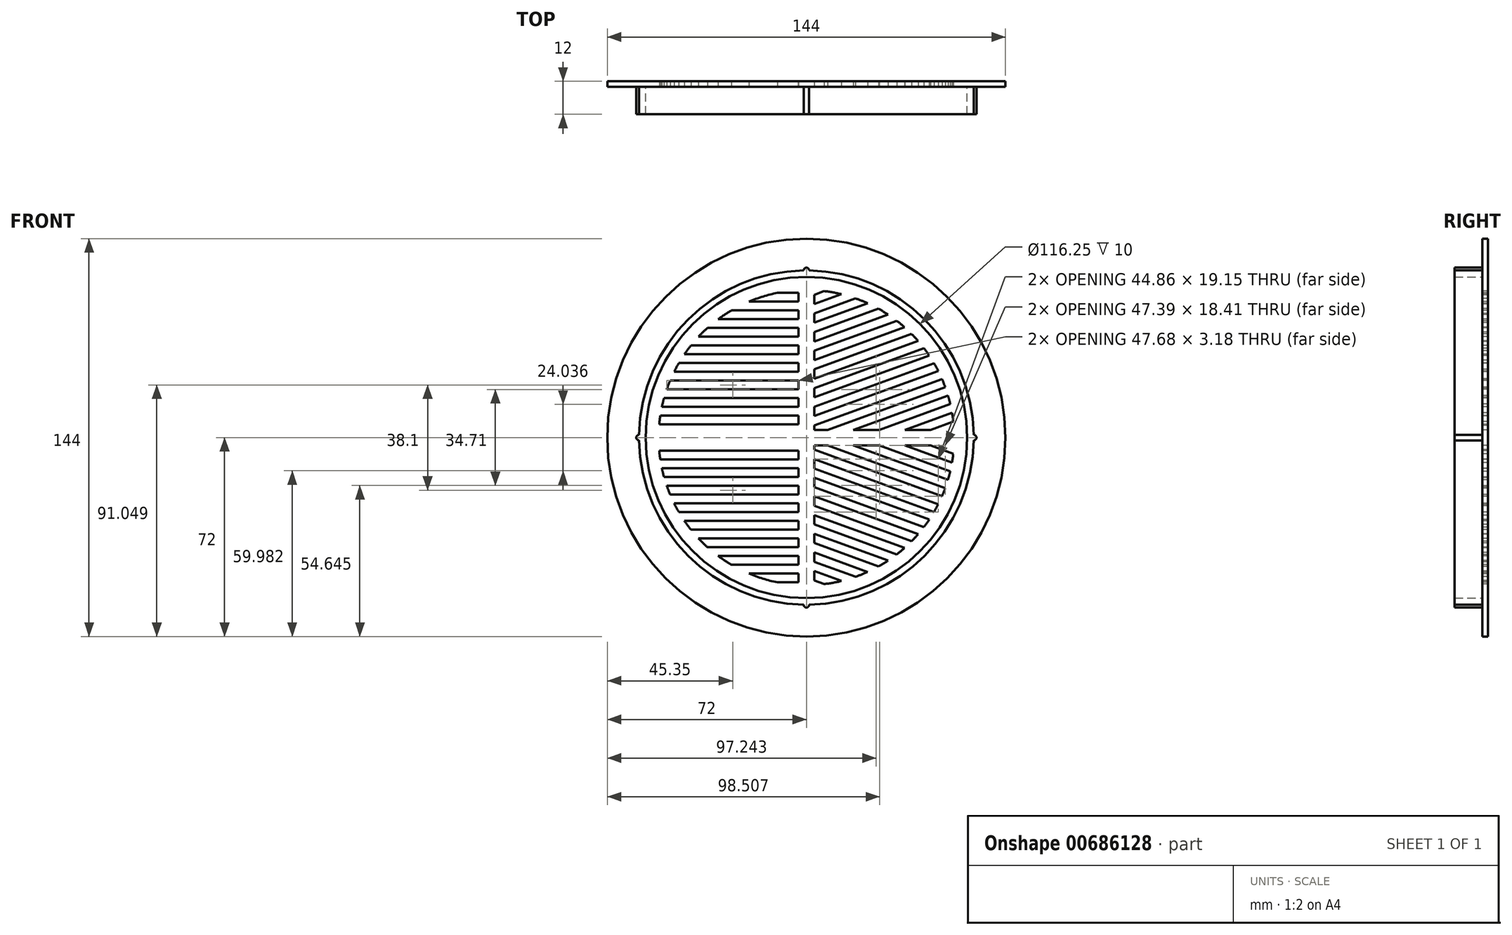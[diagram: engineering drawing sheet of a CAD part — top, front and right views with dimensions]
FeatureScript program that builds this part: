
annotation { "Feature Type Name" : "Feature", "Feature Type Description" : "" }
export const myFeature = defineFeature(function(context is Context, id is Id, definition is map)
    precondition{}
    {
        {
            var Q0;
            Q0=qCreatedBy(makeId("Front.planeOp"),FACE);
            var sketch = newSketch(context, id + "F0", { "sketchPlane" : qUnion([Q0])});
            skLineSegment(sketch, "E0", {"start": v(-20.83, -49.21) * mm, "end": v(-19.9, -49.61) * mm});
            skLineSegment(sketch, "E1", {"start": v(-19.9, -49.61) * mm, "end": v(-16.44, -50.86) * mm});
            skLineSegment(sketch, "E2", {"start": v(-16.44, -50.86) * mm, "end": v(-12.87, -51.88) * mm});
            skLineSegment(sketch, "E3", {"start": v(-12.87, -51.88) * mm, "end": v(-10.58, -52.39) * mm});
            skLineSegment(sketch, "E4", {"start": v(-10.58, -52.39) * mm, "end": v(-2.81, -52.39) * mm});
            skLineSegment(sketch, "E5", {"start": v(-2.81, -52.39) * mm, "end": v(-2.81, -49.21) * mm});
            skLineSegment(sketch, "E6", {"start": v(-2.81, -49.21) * mm, "end": v(-20.83, -49.21) * mm});
            skLineSegment(sketch, "E7", {"start": v(2.81, -48.33) * mm, "end": v(2.81, -51.7) * mm});
            skLineSegment(sketch, "E8", {"start": v(2.81, -51.7) * mm, "end": v(6.62, -53.1) * mm});
            skLineSegment(sketch, "E9", {"start": v(6.62, -53.1) * mm, "end": v(7.87, -52.94) * mm});
            skLineSegment(sketch, "E10", {"start": v(7.87, -52.94) * mm, "end": v(10.35, -52.52) * mm});
            skLineSegment(sketch, "E11", {"start": v(10.35, -52.52) * mm, "end": v(12.78, -51.98) * mm});
            skLineSegment(sketch, "E12", {"start": v(12.78, -51.98) * mm, "end": v(12.82, -51.97) * mm});
            skLineSegment(sketch, "E13", {"start": v(12.82, -51.97) * mm, "end": v(2.81, -48.33) * mm});
            skLineSegment(sketch, "E14", {"start": v(-31.9, -42.86) * mm, "end": v(-30.54, -43.86) * mm});
            skLineSegment(sketch, "E15", {"start": v(-30.54, -43.86) * mm, "end": v(-28.53, -45.2) * mm});
            skLineSegment(sketch, "E16", {"start": v(-28.53, -45.2) * mm, "end": v(-27.12, -46.04) * mm});
            skLineSegment(sketch, "E17", {"start": v(-27.12, -46.04) * mm, "end": v(-2.81, -46.04) * mm});
            skLineSegment(sketch, "E18", {"start": v(-2.81, -46.04) * mm, "end": v(-2.81, -42.86) * mm});
            skLineSegment(sketch, "E19", {"start": v(-2.81, -42.86) * mm, "end": v(-31.9, -42.86) * mm});
            skLineSegment(sketch, "E20", {"start": v(2.81, -41.57) * mm, "end": v(2.81, -44.95) * mm});
            skLineSegment(sketch, "E21", {"start": v(2.81, -44.95) * mm, "end": v(17.91, -50.44) * mm});
            skLineSegment(sketch, "E22", {"start": v(17.91, -50.44) * mm, "end": v(19.82, -49.74) * mm});
            skLineSegment(sketch, "E23", {"start": v(19.82, -49.74) * mm, "end": v(22.07, -48.78) * mm});
            skLineSegment(sketch, "E24", {"start": v(22.07, -48.78) * mm, "end": v(22.3, -48.66) * mm});
            skLineSegment(sketch, "E25", {"start": v(22.3, -48.66) * mm, "end": v(2.81, -41.57) * mm});
            skLineSegment(sketch, "E26", {"start": v(-39, -36.51) * mm, "end": v(-37.9, -37.67) * mm});
            skLineSegment(sketch, "E27", {"start": v(-37.9, -37.67) * mm, "end": v(-36.17, -39.34) * mm});
            skLineSegment(sketch, "E28", {"start": v(-36.17, -39.34) * mm, "end": v(-35.77, -39.69) * mm});
            skLineSegment(sketch, "E29", {"start": v(-35.77, -39.69) * mm, "end": v(-2.81, -39.69) * mm});
            skLineSegment(sketch, "E30", {"start": v(-2.81, -39.69) * mm, "end": v(-2.81, -36.51) * mm});
            skLineSegment(sketch, "E31", {"start": v(-2.81, -36.51) * mm, "end": v(-39, -36.51) * mm});
            skLineSegment(sketch, "E32", {"start": v(2.81, -34.81) * mm, "end": v(2.81, -38.2) * mm});
            skLineSegment(sketch, "E33", {"start": v(2.81, -38.2) * mm, "end": v(26.18, -46.7) * mm});
            skLineSegment(sketch, "E34", {"start": v(26.18, -46.7) * mm, "end": v(26.4, -46.58) * mm});
            skLineSegment(sketch, "E35", {"start": v(26.4, -46.58) * mm, "end": v(28.47, -45.34) * mm});
            skLineSegment(sketch, "E36", {"start": v(28.47, -45.34) * mm, "end": v(29.64, -44.57) * mm});
            skLineSegment(sketch, "E37", {"start": v(29.64, -44.57) * mm, "end": v(2.81, -34.81) * mm});
            skLineSegment(sketch, "E38", {"start": v(-44.11, -30.16) * mm, "end": v(-44.04, -30.28) * mm});
            skLineSegment(sketch, "E39", {"start": v(-44.04, -30.28) * mm, "end": v(-42.63, -32.23) * mm});
            skLineSegment(sketch, "E40", {"start": v(-42.63, -32.23) * mm, "end": v(-41.75, -33.34) * mm});
            skLineSegment(sketch, "E41", {"start": v(-41.75, -33.34) * mm, "end": v(-2.81, -33.34) * mm});
            skLineSegment(sketch, "E42", {"start": v(-2.81, -33.34) * mm, "end": v(-2.81, -30.16) * mm});
            skLineSegment(sketch, "E43", {"start": v(-2.81, -30.16) * mm, "end": v(-44.11, -30.16) * mm});
            skLineSegment(sketch, "E44", {"start": v(2.81, -28.05) * mm, "end": v(2.81, -31.43) * mm});
            skLineSegment(sketch, "E45", {"start": v(2.81, -31.43) * mm, "end": v(32.76, -42.33) * mm});
            skLineSegment(sketch, "E46", {"start": v(32.76, -42.33) * mm, "end": v(34.3, -41.1) * mm});
            skLineSegment(sketch, "E47", {"start": v(34.3, -41.1) * mm, "end": v(35.59, -39.98) * mm});
            skLineSegment(sketch, "E48", {"start": v(35.59, -39.98) * mm, "end": v(2.81, -28.05) * mm});
            skLineSegment(sketch, "E49", {"start": v(-47.85, -23.81) * mm, "end": v(-47.74, -24.04) * mm});
            skLineSegment(sketch, "E50", {"start": v(-47.74, -24.04) * mm, "end": v(-46.6, -26.18) * mm});
            skLineSegment(sketch, "E51", {"start": v(-46.6, -26.18) * mm, "end": v(-46.12, -26.99) * mm});
            skLineSegment(sketch, "E52", {"start": v(-46.12, -26.99) * mm, "end": v(-2.81, -26.99) * mm});
            skLineSegment(sketch, "E53", {"start": v(-2.81, -26.99) * mm, "end": v(-2.81, -23.81) * mm});
            skLineSegment(sketch, "E54", {"start": v(-2.81, -23.81) * mm, "end": v(-47.85, -23.81) * mm});
            skLineSegment(sketch, "E55", {"start": v(2.81, -21.3) * mm, "end": v(2.81, -24.67) * mm});
            skLineSegment(sketch, "E56", {"start": v(2.81, -24.67) * mm, "end": v(38.16, -37.54) * mm});
            skLineSegment(sketch, "E57", {"start": v(38.16, -37.54) * mm, "end": v(39.52, -36.12) * mm});
            skLineSegment(sketch, "E58", {"start": v(39.52, -36.12) * mm, "end": v(40.49, -35) * mm});
            skLineSegment(sketch, "E59", {"start": v(40.49, -35) * mm, "end": v(2.81, -21.3) * mm});
            skLineSegment(sketch, "E60", {"start": v(-50.52, -17.46) * mm, "end": v(-49.73, -19.6) * mm});
            skLineSegment(sketch, "E61", {"start": v(-49.73, -19.6) * mm, "end": v(-49.3, -20.64) * mm});
            skLineSegment(sketch, "E62", {"start": v(-49.3, -20.64) * mm, "end": v(-2.81, -20.64) * mm});
            skLineSegment(sketch, "E63", {"start": v(-2.81, -20.64) * mm, "end": v(-2.81, -17.46) * mm});
            skLineSegment(sketch, "E64", {"start": v(-2.81, -17.46) * mm, "end": v(-50.52, -17.46) * mm});
            skLineSegment(sketch, "E65", {"start": v(2.81, -14.54) * mm, "end": v(2.81, -17.92) * mm});
            skLineSegment(sketch, "E66", {"start": v(2.81, -17.92) * mm, "end": v(42.62, -32.4) * mm});
            skLineSegment(sketch, "E67", {"start": v(42.62, -32.4) * mm, "end": v(44.02, -30.48) * mm});
            skLineSegment(sketch, "E68", {"start": v(44.02, -30.48) * mm, "end": v(44.52, -29.72) * mm});
            skLineSegment(sketch, "E69", {"start": v(44.52, -29.72) * mm, "end": v(2.81, -14.54) * mm});
            skLineSegment(sketch, "E70", {"start": v(-52.27, -11.11) * mm, "end": v(-51.96, -12.55) * mm});
            skLineSegment(sketch, "E71", {"start": v(-51.96, -12.55) * mm, "end": v(-51.5, -14.29) * mm});
            skLineSegment(sketch, "E72", {"start": v(-51.5, -14.29) * mm, "end": v(-2.81, -14.29) * mm});
            skLineSegment(sketch, "E73", {"start": v(-2.81, -14.29) * mm, "end": v(-2.81, -11.11) * mm});
            skLineSegment(sketch, "E74", {"start": v(-2.81, -11.11) * mm, "end": v(-52.27, -11.11) * mm});
            skLineSegment(sketch, "E75", {"start": v(2.81, -7.78) * mm, "end": v(2.81, -11.16) * mm});
            skLineSegment(sketch, "E76", {"start": v(2.81, -11.16) * mm, "end": v(46.24, -26.97) * mm});
            skLineSegment(sketch, "E77", {"start": v(46.24, -26.97) * mm, "end": v(46.58, -26.4) * mm});
            skLineSegment(sketch, "E78", {"start": v(46.58, -26.4) * mm, "end": v(47.73, -24.26) * mm});
            skLineSegment(sketch, "E79", {"start": v(47.73, -24.26) * mm, "end": v(47.78, -24.15) * mm});
            skLineSegment(sketch, "E80", {"start": v(47.78, -24.15) * mm, "end": v(2.81, -7.78) * mm});
            skLineSegment(sketch, "E81", {"start": v(-53.22, -4.76) * mm, "end": v(-53.2, -5.13) * mm});
            skLineSegment(sketch, "E82", {"start": v(-53.2, -5.13) * mm, "end": v(-52.9, -7.64) * mm});
            skLineSegment(sketch, "E83", {"start": v(-52.9, -7.64) * mm, "end": v(-52.85, -7.94) * mm});
            skLineSegment(sketch, "E84", {"start": v(-52.85, -7.94) * mm, "end": v(-2.81, -7.94) * mm});
            skLineSegment(sketch, "E85", {"start": v(-2.81, -7.94) * mm, "end": v(-2.81, -4.76) * mm});
            skLineSegment(sketch, "E86", {"start": v(-2.81, -4.76) * mm, "end": v(-53.22, -4.76) * mm});
            skLineSegment(sketch, "E87", {"start": v(35.58, -2.81) * mm, "end": v(52.74, -9.06) * mm});
            skLineSegment(sketch, "E88", {"start": v(52.74, -9.06) * mm, "end": v(52.94, -7.87) * mm});
            skLineSegment(sketch, "E89", {"start": v(52.94, -7.87) * mm, "end": v(53.19, -5.84) * mm});
            skLineSegment(sketch, "E90", {"start": v(53.19, -5.84) * mm, "end": v(44.86, -2.81) * mm});
            skLineSegment(sketch, "E91", {"start": v(44.86, -2.81) * mm, "end": v(35.58, -2.81) * mm});
            skLineSegment(sketch, "E92", {"start": v(17, -2.81) * mm, "end": v(51.3, -15.3) * mm});
            skLineSegment(sketch, "E93", {"start": v(51.3, -15.3) * mm, "end": v(51.34, -15.18) * mm});
            skLineSegment(sketch, "E94", {"start": v(51.34, -15.18) * mm, "end": v(51.98, -12.78) * mm});
            skLineSegment(sketch, "E95", {"start": v(51.98, -12.78) * mm, "end": v(52.1, -12.2) * mm});
            skLineSegment(sketch, "E96", {"start": v(52.1, -12.2) * mm, "end": v(26.3, -2.81) * mm});
            skLineSegment(sketch, "E97", {"start": v(26.3, -2.81) * mm, "end": v(17, -2.81) * mm});
            skLineSegment(sketch, "E98", {"start": v(2.81, -2.81) * mm, "end": v(2.81, -4.4) * mm});
            skLineSegment(sketch, "E99", {"start": v(2.81, -4.4) * mm, "end": v(49.12, -21.26) * mm});
            skLineSegment(sketch, "E100", {"start": v(49.12, -21.26) * mm, "end": v(49.74, -19.82) * mm});
            skLineSegment(sketch, "E101", {"start": v(49.74, -19.82) * mm, "end": v(50.3, -18.3) * mm});
            skLineSegment(sketch, "E102", {"start": v(50.3, -18.3) * mm, "end": v(7.73, -2.81) * mm});
            skLineSegment(sketch, "E103", {"start": v(7.73, -2.81) * mm, "end": v(2.81, -2.81) * mm});
            skLineSegment(sketch, "E104", {"start": v(-53.4, 1.59) * mm, "end": v(-53.44, 0) * mm});
            skLineSegment(sketch, "E105", {"start": v(-53.44, 0) * mm, "end": v(-53.4, -1.59) * mm});
            skLineSegment(sketch, "E106", {"start": v(-53.4, -1.59) * mm, "end": v(-2.81, -1.59) * mm});
            skLineSegment(sketch, "E107", {"start": v(-2.81, -1.59) * mm, "end": v(-2.81, 1.59) * mm});
            skLineSegment(sketch, "E108", {"start": v(-2.81, 1.59) * mm, "end": v(-53.4, 1.59) * mm});
            skLineSegment(sketch, "E109", {"start": v(-52.85, 7.94) * mm, "end": v(-52.9, 7.64) * mm});
            skLineSegment(sketch, "E110", {"start": v(-52.9, 7.64) * mm, "end": v(-53.2, 5.13) * mm});
            skLineSegment(sketch, "E111", {"start": v(-53.2, 5.13) * mm, "end": v(-53.22, 4.76) * mm});
            skLineSegment(sketch, "E112", {"start": v(-53.22, 4.76) * mm, "end": v(-2.81, 4.76) * mm});
            skLineSegment(sketch, "E113", {"start": v(-2.81, 4.76) * mm, "end": v(-2.81, 7.94) * mm});
            skLineSegment(sketch, "E114", {"start": v(-2.81, 7.94) * mm, "end": v(-52.85, 7.94) * mm});
            skLineSegment(sketch, "E115", {"start": v(52.74, 9.06) * mm, "end": v(35.58, 2.81) * mm});
            skLineSegment(sketch, "E116", {"start": v(35.58, 2.81) * mm, "end": v(44.86, 2.81) * mm});
            skLineSegment(sketch, "E117", {"start": v(44.86, 2.81) * mm, "end": v(53.19, 5.84) * mm});
            skLineSegment(sketch, "E118", {"start": v(53.19, 5.84) * mm, "end": v(52.94, 7.87) * mm});
            skLineSegment(sketch, "E119", {"start": v(52.94, 7.87) * mm, "end": v(52.74, 9.06) * mm});
            skLineSegment(sketch, "E120", {"start": v(-51.5, 14.29) * mm, "end": v(-51.96, 12.55) * mm});
            skLineSegment(sketch, "E121", {"start": v(-51.96, 12.55) * mm, "end": v(-52.27, 11.11) * mm});
            skLineSegment(sketch, "E122", {"start": v(-52.27, 11.11) * mm, "end": v(-2.81, 11.11) * mm});
            skLineSegment(sketch, "E123", {"start": v(-2.81, 11.11) * mm, "end": v(-2.81, 14.29) * mm});
            skLineSegment(sketch, "E124", {"start": v(-2.81, 14.29) * mm, "end": v(-51.5, 14.29) * mm});
            skLineSegment(sketch, "E125", {"start": v(51.3, 15.3) * mm, "end": v(17, 2.81) * mm});
            skLineSegment(sketch, "E126", {"start": v(17, 2.81) * mm, "end": v(26.3, 2.81) * mm});
            skLineSegment(sketch, "E127", {"start": v(26.3, 2.81) * mm, "end": v(52.1, 12.2) * mm});
            skLineSegment(sketch, "E128", {"start": v(52.1, 12.2) * mm, "end": v(51.98, 12.78) * mm});
            skLineSegment(sketch, "E129", {"start": v(51.98, 12.78) * mm, "end": v(51.34, 15.18) * mm});
            skLineSegment(sketch, "E130", {"start": v(51.34, 15.18) * mm, "end": v(51.3, 15.3) * mm});
            skLineSegment(sketch, "E131", {"start": v(-49.3, 20.64) * mm, "end": v(-49.73, 19.6) * mm});
            skLineSegment(sketch, "E132", {"start": v(-49.73, 19.6) * mm, "end": v(-50.52, 17.46) * mm});
            skLineSegment(sketch, "E133", {"start": v(-50.52, 17.46) * mm, "end": v(-2.81, 17.46) * mm});
            skLineSegment(sketch, "E134", {"start": v(-2.81, 17.46) * mm, "end": v(-2.81, 20.64) * mm});
            skLineSegment(sketch, "E135", {"start": v(-2.81, 20.64) * mm, "end": v(-49.3, 20.64) * mm});
            skLineSegment(sketch, "E136", {"start": v(49.12, 21.26) * mm, "end": v(2.81, 4.4) * mm});
            skLineSegment(sketch, "E137", {"start": v(2.81, 4.4) * mm, "end": v(2.81, 2.81) * mm});
            skLineSegment(sketch, "E138", {"start": v(2.81, 2.81) * mm, "end": v(7.73, 2.81) * mm});
            skLineSegment(sketch, "E139", {"start": v(7.73, 2.81) * mm, "end": v(50.3, 18.3) * mm});
            skLineSegment(sketch, "E140", {"start": v(50.3, 18.3) * mm, "end": v(49.74, 19.82) * mm});
            skLineSegment(sketch, "E141", {"start": v(49.74, 19.82) * mm, "end": v(49.12, 21.26) * mm});
            skLineSegment(sketch, "E142", {"start": v(46.24, 26.97) * mm, "end": v(2.81, 11.16) * mm});
            skLineSegment(sketch, "E143", {"start": v(2.81, 11.16) * mm, "end": v(2.81, 7.78) * mm});
            skLineSegment(sketch, "E144", {"start": v(2.81, 7.78) * mm, "end": v(47.78, 24.15) * mm});
            skLineSegment(sketch, "E145", {"start": v(47.78, 24.15) * mm, "end": v(47.73, 24.26) * mm});
            skLineSegment(sketch, "E146", {"start": v(47.73, 24.26) * mm, "end": v(46.58, 26.4) * mm});
            skLineSegment(sketch, "E147", {"start": v(46.58, 26.4) * mm, "end": v(46.24, 26.97) * mm});
            skLineSegment(sketch, "E148", {"start": v(-46.12, 26.99) * mm, "end": v(-46.6, 26.18) * mm});
            skLineSegment(sketch, "E149", {"start": v(-46.6, 26.18) * mm, "end": v(-47.74, 24.04) * mm});
            skLineSegment(sketch, "E150", {"start": v(-47.74, 24.04) * mm, "end": v(-47.85, 23.81) * mm});
            skLineSegment(sketch, "E151", {"start": v(-47.85, 23.81) * mm, "end": v(-2.81, 23.81) * mm});
            skLineSegment(sketch, "E152", {"start": v(-2.81, 23.81) * mm, "end": v(-2.81, 26.99) * mm});
            skLineSegment(sketch, "E153", {"start": v(-2.81, 26.99) * mm, "end": v(-46.12, 26.99) * mm});
            skLineSegment(sketch, "E154", {"start": v(42.62, 32.4) * mm, "end": v(2.81, 17.92) * mm});
            skLineSegment(sketch, "E155", {"start": v(2.81, 17.92) * mm, "end": v(2.81, 14.54) * mm});
            skLineSegment(sketch, "E156", {"start": v(2.81, 14.54) * mm, "end": v(44.52, 29.72) * mm});
            skLineSegment(sketch, "E157", {"start": v(44.52, 29.72) * mm, "end": v(44.02, 30.48) * mm});
            skLineSegment(sketch, "E158", {"start": v(44.02, 30.48) * mm, "end": v(42.62, 32.4) * mm});
            skLineSegment(sketch, "E159", {"start": v(-41.75, 33.34) * mm, "end": v(-42.63, 32.23) * mm});
            skLineSegment(sketch, "E160", {"start": v(-42.63, 32.23) * mm, "end": v(-44.04, 30.28) * mm});
            skLineSegment(sketch, "E161", {"start": v(-44.04, 30.28) * mm, "end": v(-44.11, 30.16) * mm});
            skLineSegment(sketch, "E162", {"start": v(-44.11, 30.16) * mm, "end": v(-2.81, 30.16) * mm});
            skLineSegment(sketch, "E163", {"start": v(-2.81, 30.16) * mm, "end": v(-2.81, 33.34) * mm});
            skLineSegment(sketch, "E164", {"start": v(-2.81, 33.34) * mm, "end": v(-41.75, 33.34) * mm});
            skLineSegment(sketch, "E165", {"start": v(38.16, 37.54) * mm, "end": v(2.81, 24.67) * mm});
            skLineSegment(sketch, "E166", {"start": v(2.81, 24.67) * mm, "end": v(2.81, 21.3) * mm});
            skLineSegment(sketch, "E167", {"start": v(2.81, 21.3) * mm, "end": v(40.49, 35) * mm});
            skLineSegment(sketch, "E168", {"start": v(40.49, 35) * mm, "end": v(39.52, 36.12) * mm});
            skLineSegment(sketch, "E169", {"start": v(39.52, 36.12) * mm, "end": v(38.16, 37.54) * mm});
            skLineSegment(sketch, "E170", {"start": v(-35.77, 39.69) * mm, "end": v(-36.17, 39.34) * mm});
            skLineSegment(sketch, "E171", {"start": v(-36.17, 39.34) * mm, "end": v(-37.9, 37.67) * mm});
            skLineSegment(sketch, "E172", {"start": v(-37.9, 37.67) * mm, "end": v(-39, 36.51) * mm});
            skLineSegment(sketch, "E173", {"start": v(-39, 36.51) * mm, "end": v(-2.81, 36.51) * mm});
            skLineSegment(sketch, "E174", {"start": v(-2.81, 36.51) * mm, "end": v(-2.81, 39.69) * mm});
            skLineSegment(sketch, "E175", {"start": v(-2.81, 39.69) * mm, "end": v(-35.77, 39.69) * mm});
            skLineSegment(sketch, "E176", {"start": v(32.76, 42.33) * mm, "end": v(2.81, 31.43) * mm});
            skLineSegment(sketch, "E177", {"start": v(2.81, 31.43) * mm, "end": v(2.81, 28.05) * mm});
            skLineSegment(sketch, "E178", {"start": v(2.81, 28.05) * mm, "end": v(35.59, 39.98) * mm});
            skLineSegment(sketch, "E179", {"start": v(35.59, 39.98) * mm, "end": v(34.3, 41.1) * mm});
            skLineSegment(sketch, "E180", {"start": v(34.3, 41.1) * mm, "end": v(32.76, 42.33) * mm});
            skLineSegment(sketch, "E181", {"start": v(-27.12, 46.04) * mm, "end": v(-28.53, 45.2) * mm});
            skLineSegment(sketch, "E182", {"start": v(-28.53, 45.2) * mm, "end": v(-30.54, 43.86) * mm});
            skLineSegment(sketch, "E183", {"start": v(-30.54, 43.86) * mm, "end": v(-31.9, 42.86) * mm});
            skLineSegment(sketch, "E184", {"start": v(-31.9, 42.86) * mm, "end": v(-2.81, 42.86) * mm});
            skLineSegment(sketch, "E185", {"start": v(-2.81, 42.86) * mm, "end": v(-2.81, 46.04) * mm});
            skLineSegment(sketch, "E186", {"start": v(-2.81, 46.04) * mm, "end": v(-27.12, 46.04) * mm});
            skLineSegment(sketch, "E187", {"start": v(26.18, 46.7) * mm, "end": v(2.81, 38.2) * mm});
            skLineSegment(sketch, "E188", {"start": v(2.81, 38.2) * mm, "end": v(2.81, 34.81) * mm});
            skLineSegment(sketch, "E189", {"start": v(2.81, 34.81) * mm, "end": v(29.64, 44.57) * mm});
            skLineSegment(sketch, "E190", {"start": v(29.71, 44.6) * mm, "end": v(26.4, 46.58) * mm});
            skLineSegment(sketch, "E191", {"start": v(17.91, 50.44) * mm, "end": v(2.81, 44.95) * mm});
            skLineSegment(sketch, "E192", {"start": v(2.81, 44.95) * mm, "end": v(2.81, 41.57) * mm});
            skLineSegment(sketch, "E193", {"start": v(2.81, 41.57) * mm, "end": v(22.3, 48.66) * mm});
            skLineSegment(sketch, "E194", {"start": v(22.3, 48.66) * mm, "end": v(22.07, 48.78) * mm});
            skLineSegment(sketch, "E195", {"start": v(22.07, 48.78) * mm, "end": v(19.82, 49.74) * mm});
            skLineSegment(sketch, "E196", {"start": v(19.82, 49.74) * mm, "end": v(17.91, 50.44) * mm});
            skLineSegment(sketch, "E197", {"start": v(-10.58, 52.39) * mm, "end": v(-12.87, 51.88) * mm});
            skLineSegment(sketch, "E198", {"start": v(-12.87, 51.88) * mm, "end": v(-16.44, 50.86) * mm});
            skLineSegment(sketch, "E199", {"start": v(-16.44, 50.86) * mm, "end": v(-19.9, 49.6) * mm});
            skLineSegment(sketch, "E200", {"start": v(-19.9, 49.6) * mm, "end": v(-20.83, 49.21) * mm});
            skLineSegment(sketch, "E201", {"start": v(-20.83, 49.21) * mm, "end": v(-2.81, 49.21) * mm});
            skLineSegment(sketch, "E202", {"start": v(-2.81, 49.21) * mm, "end": v(-2.81, 52.39) * mm});
            skLineSegment(sketch, "E203", {"start": v(-2.81, 52.39) * mm, "end": v(-10.58, 52.39) * mm});
            skLineSegment(sketch, "E204", {"start": v(6.62, 53.1) * mm, "end": v(2.81, 51.7) * mm});
            skLineSegment(sketch, "E205", {"start": v(2.81, 51.7) * mm, "end": v(2.81, 48.33) * mm});
            skLineSegment(sketch, "E206", {"start": v(2.81, 48.33) * mm, "end": v(12.82, 51.97) * mm});
            skLineSegment(sketch, "E207", {"start": v(12.82, 51.97) * mm, "end": v(12.78, 51.98) * mm});
            skLineSegment(sketch, "E208", {"start": v(12.78, 51.98) * mm, "end": v(10.35, 52.52) * mm});
            skLineSegment(sketch, "E209", {"start": v(10.35, 52.52) * mm, "end": v(7.87, 52.94) * mm});
            skLineSegment(sketch, "E210", {"start": v(7.87, 52.94) * mm, "end": v(6.62, 53.1) * mm});
            skLineSegment(sketch, "E211", {"start": v(0, 58.13) * mm, "end": v(3, 58.05) * mm});
            skLineSegment(sketch, "E212", {"start": v(3, 58.05) * mm, "end": v(5.94, 57.82) * mm});
            skLineSegment(sketch, "E213", {"start": v(5.94, 57.82) * mm, "end": v(8.85, 57.45) * mm});
            skLineSegment(sketch, "E214", {"start": v(8.85, 57.45) * mm, "end": v(11.71, 56.94) * mm});
            skLineSegment(sketch, "E215", {"start": v(11.71, 56.94) * mm, "end": v(14.53, 56.3) * mm});
            skLineSegment(sketch, "E216", {"start": v(14.53, 56.3) * mm, "end": v(17.28, 55.51) * mm});
            skLineSegment(sketch, "E217", {"start": v(17.28, 55.51) * mm, "end": v(19.98, 54.6) * mm});
            skLineSegment(sketch, "E218", {"start": v(19.98, 54.6) * mm, "end": v(22.63, 53.56) * mm});
            skLineSegment(sketch, "E219", {"start": v(22.63, 53.56) * mm, "end": v(25.2, 52.4) * mm});
            skLineSegment(sketch, "E220", {"start": v(25.2, 52.4) * mm, "end": v(27.7, 51.1) * mm});
            skLineSegment(sketch, "E221", {"start": v(27.7, 51.1) * mm, "end": v(30.14, 49.71) * mm});
            skLineSegment(sketch, "E222", {"start": v(30.14, 49.71) * mm, "end": v(32.5, 48.2) * mm});
            skLineSegment(sketch, "E223", {"start": v(32.5, 48.2) * mm, "end": v(34.78, 46.58) * mm});
            skLineSegment(sketch, "E224", {"start": v(34.78, 46.58) * mm, "end": v(36.97, 44.85) * mm});
            skLineSegment(sketch, "E225", {"start": v(36.97, 44.85) * mm, "end": v(39.08, 43.03) * mm});
            skLineSegment(sketch, "E226", {"start": v(39.08, 43.03) * mm, "end": v(41.1, 41.1) * mm});
            skLineSegment(sketch, "E227", {"start": v(41.1, 41.1) * mm, "end": v(43.03, 39.08) * mm});
            skLineSegment(sketch, "E228", {"start": v(43.03, 39.08) * mm, "end": v(44.85, 36.97) * mm});
            skLineSegment(sketch, "E229", {"start": v(44.85, 36.97) * mm, "end": v(46.58, 34.78) * mm});
            skLineSegment(sketch, "E230", {"start": v(46.58, 34.78) * mm, "end": v(48.2, 32.5) * mm});
            skLineSegment(sketch, "E231", {"start": v(48.2, 32.5) * mm, "end": v(49.71, 30.14) * mm});
            skLineSegment(sketch, "E232", {"start": v(49.71, 30.14) * mm, "end": v(51.1, 27.7) * mm});
            skLineSegment(sketch, "E233", {"start": v(51.1, 27.7) * mm, "end": v(52.4, 25.2) * mm});
            skLineSegment(sketch, "E234", {"start": v(52.4, 25.2) * mm, "end": v(53.56, 22.63) * mm});
            skLineSegment(sketch, "E235", {"start": v(53.56, 22.63) * mm, "end": v(54.6, 19.99) * mm});
            skLineSegment(sketch, "E236", {"start": v(54.6, 19.99) * mm, "end": v(55.51, 17.28) * mm});
            skLineSegment(sketch, "E237", {"start": v(55.51, 17.28) * mm, "end": v(56.3, 14.53) * mm});
            skLineSegment(sketch, "E238", {"start": v(56.3, 14.53) * mm, "end": v(56.94, 11.71) * mm});
            skLineSegment(sketch, "E239", {"start": v(56.94, 11.71) * mm, "end": v(57.46, 8.85) * mm});
            skLineSegment(sketch, "E240", {"start": v(57.46, 8.85) * mm, "end": v(57.82, 5.94) * mm});
            skLineSegment(sketch, "E241", {"start": v(57.82, 5.94) * mm, "end": v(58.05, 3) * mm});
            skLineSegment(sketch, "E242", {"start": v(58.05, 3) * mm, "end": v(58.12, 0) * mm});
            skLineSegment(sketch, "E243", {"start": v(58.12, 0) * mm, "end": v(58.05, -3) * mm});
            skLineSegment(sketch, "E244", {"start": v(58.05, -3) * mm, "end": v(57.82, -5.94) * mm});
            skLineSegment(sketch, "E245", {"start": v(57.82, -5.94) * mm, "end": v(57.46, -8.85) * mm});
            skLineSegment(sketch, "E246", {"start": v(57.46, -8.85) * mm, "end": v(56.94, -11.71) * mm});
            skLineSegment(sketch, "E247", {"start": v(56.94, -11.71) * mm, "end": v(56.3, -14.53) * mm});
            skLineSegment(sketch, "E248", {"start": v(56.3, -14.53) * mm, "end": v(55.51, -17.28) * mm});
            skLineSegment(sketch, "E249", {"start": v(55.51, -17.28) * mm, "end": v(54.6, -19.99) * mm});
            skLineSegment(sketch, "E250", {"start": v(54.6, -19.99) * mm, "end": v(53.56, -22.63) * mm});
            skLineSegment(sketch, "E251", {"start": v(53.56, -22.63) * mm, "end": v(52.4, -25.2) * mm});
            skLineSegment(sketch, "E252", {"start": v(52.4, -25.2) * mm, "end": v(51.1, -27.7) * mm});
            skLineSegment(sketch, "E253", {"start": v(51.1, -27.7) * mm, "end": v(49.71, -30.14) * mm});
            skLineSegment(sketch, "E254", {"start": v(49.71, -30.14) * mm, "end": v(48.2, -32.5) * mm});
            skLineSegment(sketch, "E255", {"start": v(48.2, -32.5) * mm, "end": v(46.58, -34.78) * mm});
            skLineSegment(sketch, "E256", {"start": v(46.58, -34.78) * mm, "end": v(44.85, -36.97) * mm});
            skLineSegment(sketch, "E257", {"start": v(44.85, -36.97) * mm, "end": v(43.03, -39.08) * mm});
            skLineSegment(sketch, "E258", {"start": v(43.03, -39.08) * mm, "end": v(41.1, -41.1) * mm});
            skLineSegment(sketch, "E259", {"start": v(41.1, -41.1) * mm, "end": v(39.08, -43.03) * mm});
            skLineSegment(sketch, "E260", {"start": v(39.08, -43.03) * mm, "end": v(36.97, -44.85) * mm});
            skLineSegment(sketch, "E261", {"start": v(36.97, -44.85) * mm, "end": v(34.78, -46.58) * mm});
            skLineSegment(sketch, "E262", {"start": v(34.78, -46.58) * mm, "end": v(32.5, -48.2) * mm});
            skLineSegment(sketch, "E263", {"start": v(32.5, -48.2) * mm, "end": v(30.14, -49.71) * mm});
            skLineSegment(sketch, "E264", {"start": v(30.14, -49.71) * mm, "end": v(27.7, -51.1) * mm});
            skLineSegment(sketch, "E265", {"start": v(27.7, -51.1) * mm, "end": v(25.2, -52.4) * mm});
            skLineSegment(sketch, "E266", {"start": v(25.2, -52.4) * mm, "end": v(22.63, -53.56) * mm});
            skLineSegment(sketch, "E267", {"start": v(22.63, -53.56) * mm, "end": v(19.98, -54.6) * mm});
            skLineSegment(sketch, "E268", {"start": v(19.98, -54.6) * mm, "end": v(17.28, -55.51) * mm});
            skLineSegment(sketch, "E269", {"start": v(17.28, -55.51) * mm, "end": v(14.53, -56.3) * mm});
            skLineSegment(sketch, "E270", {"start": v(14.53, -56.3) * mm, "end": v(11.71, -56.94) * mm});
            skLineSegment(sketch, "E271", {"start": v(11.71, -56.94) * mm, "end": v(8.85, -57.46) * mm});
            skLineSegment(sketch, "E272", {"start": v(8.85, -57.46) * mm, "end": v(5.94, -57.82) * mm});
            skLineSegment(sketch, "E273", {"start": v(5.94, -57.82) * mm, "end": v(3, -58.05) * mm});
            skLineSegment(sketch, "E274", {"start": v(3, -58.05) * mm, "end": v(0, -58.13) * mm});
            skLineSegment(sketch, "E275", {"start": v(0, -58.13) * mm, "end": v(-3, -58.05) * mm});
            skLineSegment(sketch, "E276", {"start": v(-3, -58.05) * mm, "end": v(-5.94, -57.82) * mm});
            skLineSegment(sketch, "E277", {"start": v(-5.94, -57.82) * mm, "end": v(-8.85, -57.46) * mm});
            skLineSegment(sketch, "E278", {"start": v(-8.85, -57.46) * mm, "end": v(-11.71, -56.94) * mm});
            skLineSegment(sketch, "E279", {"start": v(-11.71, -56.94) * mm, "end": v(-14.53, -56.3) * mm});
            skLineSegment(sketch, "E280", {"start": v(-14.53, -56.3) * mm, "end": v(-17.28, -55.51) * mm});
            skLineSegment(sketch, "E281", {"start": v(-17.28, -55.51) * mm, "end": v(-19.98, -54.6) * mm});
            skLineSegment(sketch, "E282", {"start": v(-19.98, -54.6) * mm, "end": v(-22.63, -53.56) * mm});
            skLineSegment(sketch, "E283", {"start": v(-22.63, -53.56) * mm, "end": v(-25.2, -52.4) * mm});
            skLineSegment(sketch, "E284", {"start": v(-25.2, -52.4) * mm, "end": v(-27.7, -51.1) * mm});
            skLineSegment(sketch, "E285", {"start": v(-27.7, -51.1) * mm, "end": v(-30.14, -49.71) * mm});
            skLineSegment(sketch, "E286", {"start": v(-30.14, -49.71) * mm, "end": v(-32.5, -48.2) * mm});
            skLineSegment(sketch, "E287", {"start": v(-32.5, -48.2) * mm, "end": v(-34.78, -46.58) * mm});
            skLineSegment(sketch, "E288", {"start": v(-34.78, -46.58) * mm, "end": v(-36.97, -44.85) * mm});
            skLineSegment(sketch, "E289", {"start": v(-36.97, -44.85) * mm, "end": v(-39.08, -43.03) * mm});
            skLineSegment(sketch, "E290", {"start": v(-39.08, -43.03) * mm, "end": v(-41.1, -41.1) * mm});
            skLineSegment(sketch, "E291", {"start": v(-41.1, -41.1) * mm, "end": v(-43.03, -39.08) * mm});
            skLineSegment(sketch, "E292", {"start": v(-43.03, -39.08) * mm, "end": v(-44.85, -36.97) * mm});
            skLineSegment(sketch, "E293", {"start": v(-44.85, -36.97) * mm, "end": v(-46.58, -34.78) * mm});
            skLineSegment(sketch, "E294", {"start": v(-46.58, -34.78) * mm, "end": v(-48.2, -32.5) * mm});
            skLineSegment(sketch, "E295", {"start": v(-48.2, -32.5) * mm, "end": v(-49.71, -30.14) * mm});
            skLineSegment(sketch, "E296", {"start": v(-49.71, -30.14) * mm, "end": v(-51.1, -27.7) * mm});
            skLineSegment(sketch, "E297", {"start": v(-51.1, -27.7) * mm, "end": v(-52.4, -25.2) * mm});
            skLineSegment(sketch, "E298", {"start": v(-52.4, -25.2) * mm, "end": v(-53.56, -22.63) * mm});
            skLineSegment(sketch, "E299", {"start": v(-53.56, -22.63) * mm, "end": v(-54.6, -19.99) * mm});
            skLineSegment(sketch, "E300", {"start": v(-54.6, -19.99) * mm, "end": v(-55.51, -17.28) * mm});
            skLineSegment(sketch, "E301", {"start": v(-55.51, -17.28) * mm, "end": v(-56.3, -14.53) * mm});
            skLineSegment(sketch, "E302", {"start": v(-56.3, -14.53) * mm, "end": v(-56.94, -11.71) * mm});
            skLineSegment(sketch, "E303", {"start": v(-56.94, -11.71) * mm, "end": v(-57.46, -8.85) * mm});
            skLineSegment(sketch, "E304", {"start": v(-57.46, -8.85) * mm, "end": v(-57.82, -5.94) * mm});
            skLineSegment(sketch, "E305", {"start": v(-57.82, -5.94) * mm, "end": v(-58.05, -3) * mm});
            skLineSegment(sketch, "E306", {"start": v(-58.05, -3) * mm, "end": v(-58.12, 0) * mm});
            skLineSegment(sketch, "E307", {"start": v(-58.12, 0) * mm, "end": v(-58.05, 3) * mm});
            skLineSegment(sketch, "E308", {"start": v(-58.05, 3) * mm, "end": v(-57.82, 5.94) * mm});
            skLineSegment(sketch, "E309", {"start": v(-57.82, 5.94) * mm, "end": v(-57.46, 8.85) * mm});
            skLineSegment(sketch, "E310", {"start": v(-57.46, 8.85) * mm, "end": v(-56.94, 11.71) * mm});
            skLineSegment(sketch, "E311", {"start": v(-56.94, 11.71) * mm, "end": v(-56.3, 14.53) * mm});
            skLineSegment(sketch, "E312", {"start": v(-56.3, 14.53) * mm, "end": v(-55.51, 17.28) * mm});
            skLineSegment(sketch, "E313", {"start": v(-55.51, 17.28) * mm, "end": v(-54.6, 19.99) * mm});
            skLineSegment(sketch, "E314", {"start": v(-54.6, 19.99) * mm, "end": v(-53.56, 22.63) * mm});
            skLineSegment(sketch, "E315", {"start": v(-53.56, 22.63) * mm, "end": v(-52.4, 25.2) * mm});
            skLineSegment(sketch, "E316", {"start": v(-52.4, 25.2) * mm, "end": v(-51.1, 27.7) * mm});
            skLineSegment(sketch, "E317", {"start": v(-51.1, 27.7) * mm, "end": v(-49.71, 30.14) * mm});
            skLineSegment(sketch, "E318", {"start": v(-49.71, 30.14) * mm, "end": v(-48.2, 32.5) * mm});
            skLineSegment(sketch, "E319", {"start": v(-48.2, 32.5) * mm, "end": v(-46.58, 34.78) * mm});
            skLineSegment(sketch, "E320", {"start": v(-46.58, 34.78) * mm, "end": v(-44.85, 36.97) * mm});
            skLineSegment(sketch, "E321", {"start": v(-44.85, 36.97) * mm, "end": v(-43.03, 39.08) * mm});
            skLineSegment(sketch, "E322", {"start": v(-43.03, 39.08) * mm, "end": v(-41.1, 41.1) * mm});
            skLineSegment(sketch, "E323", {"start": v(-41.1, 41.1) * mm, "end": v(-39.08, 43.03) * mm});
            skLineSegment(sketch, "E324", {"start": v(-39.08, 43.03) * mm, "end": v(-36.97, 44.85) * mm});
            skLineSegment(sketch, "E325", {"start": v(-36.97, 44.85) * mm, "end": v(-34.78, 46.58) * mm});
            skLineSegment(sketch, "E326", {"start": v(-34.78, 46.58) * mm, "end": v(-32.5, 48.2) * mm});
            skLineSegment(sketch, "E327", {"start": v(-32.5, 48.2) * mm, "end": v(-30.14, 49.71) * mm});
            skLineSegment(sketch, "E328", {"start": v(-30.14, 49.71) * mm, "end": v(-27.7, 51.1) * mm});
            skLineSegment(sketch, "E329", {"start": v(-27.7, 51.1) * mm, "end": v(-25.2, 52.4) * mm});
            skLineSegment(sketch, "E330", {"start": v(-25.2, 52.4) * mm, "end": v(-22.63, 53.56) * mm});
            skLineSegment(sketch, "E331", {"start": v(-22.63, 53.56) * mm, "end": v(-19.98, 54.6) * mm});
            skLineSegment(sketch, "E332", {"start": v(-19.98, 54.6) * mm, "end": v(-17.28, 55.51) * mm});
            skLineSegment(sketch, "E333", {"start": v(-17.28, 55.51) * mm, "end": v(-14.53, 56.3) * mm});
            skLineSegment(sketch, "E334", {"start": v(-14.53, 56.3) * mm, "end": v(-11.71, 56.94) * mm});
            skLineSegment(sketch, "E335", {"start": v(-11.71, 56.94) * mm, "end": v(-8.85, 57.45) * mm});
            skLineSegment(sketch, "E336", {"start": v(-8.85, 57.45) * mm, "end": v(-5.94, 57.82) * mm});
            skLineSegment(sketch, "E337", {"start": v(-5.94, 57.82) * mm, "end": v(-3, 58.05) * mm});
            skLineSegment(sketch, "E338", {"start": v(-3, 58.05) * mm, "end": v(0, 58.13) * mm});
            skCircle(sketch, "E339", {"center": v(0, 0) * mm, "radius": 58.12 * mm});
            skCircle(sketch, "E340", {"center": v(0, 0) * mm, "radius": 61.5 * mm});
            skCircle(sketch, "E341", {"center": v(0, 61.5) * mm, "radius": 0.3 * mm});
            skCircle(sketch, "E342.1.0", {"center": v(-61.5, 0) * mm, "radius": 0.3 * mm});
            skCircle(sketch, "E342.2.0", {"center": v(0, -61.5) * mm, "radius": 0.3 * mm});
            skCircle(sketch, "E342.3.0", {"center": v(61.5, 0) * mm, "radius": 0.3 * mm});
            skCircle(sketch, "E343", {"center": v(0, 0) * mm, "radius": 72 * mm});
            skSolve(sketch);
        }
        {
            var Q0;
            Q0=qCreatedBy(makeId("Front.planeOp"),FACE);
            cPlane(context, id + "F1", {"entities" : qUnion([Q0]), "cplaneType" : CPlaneType.OFFSET, "offset" : 10 * mm, "oppositeDirection" : true, "width" : 150 * mm, "height" : 150 * mm});
        }
        {
            var Q0;
            Q0=qCreatedBy(id+"F1.planeOp",FACE);
            var sketch = newSketch(context, id + "F2", { "sketchPlane" : qUnion([Q0])});
            skLineSegment(sketch, "E344.0", {"start": v(-10.58, -52.39) * mm, "end": v(-2.81, -52.39) * mm});
            skLineSegment(sketch, "E344.1", {"start": v(-2.81, -49.21) * mm, "end": v(-20.83, -49.21) * mm});
            skLineSegment(sketch, "E344.2", {"start": v(2.81, -31.43) * mm, "end": v(32.76, -42.33) * mm});
            skLineSegment(sketch, "E344.3", {"start": v(-35.77, -39.69) * mm, "end": v(-2.81, -39.69) * mm});
            skLineSegment(sketch, "E344.4", {"start": v(51.3, 15.3) * mm, "end": v(17, 2.81) * mm});
            skLineSegment(sketch, "E344.5", {"start": v(2.81, 34.81) * mm, "end": v(29.64, 44.57) * mm});
            skLineSegment(sketch, "E344.6", {"start": v(-39, 36.51) * mm, "end": v(-2.81, 36.51) * mm});
            skLineSegment(sketch, "E344.7", {"start": v(-49.3, -20.64) * mm, "end": v(-2.81, -20.64) * mm});
            skLineSegment(sketch, "E344.8", {"start": v(46.24, 26.97) * mm, "end": v(2.81, 11.16) * mm});
            skLineSegment(sketch, "E344.9", {"start": v(17, 2.81) * mm, "end": v(26.3, 2.81) * mm});
            skLineSegment(sketch, "E344.10", {"start": v(2.81, 48.33) * mm, "end": v(12.82, 51.97) * mm});
            skLineSegment(sketch, "E344.11", {"start": v(-2.81, -36.51) * mm, "end": v(-39, -36.51) * mm});
            skLineSegment(sketch, "E344.12", {"start": v(26.3, 2.81) * mm, "end": v(52.1, 12.2) * mm});
            skLineSegment(sketch, "E344.13", {"start": v(17.91, 50.44) * mm, "end": v(2.81, 44.95) * mm});
            skLineSegment(sketch, "E344.14", {"start": v(-2.81, 39.69) * mm, "end": v(-2.81, 39.69) * mm});
            skLineSegment(sketch, "E344.15", {"start": v(2.81, 7.78) * mm, "end": v(47.78, 24.15) * mm});
            skLineSegment(sketch, "E344.16", {"start": v(-53.22, 4.76) * mm, "end": v(-2.81, 4.76) * mm});
            skLineSegment(sketch, "E344.17", {"start": v(52.1, -12.2) * mm, "end": v(26.3, -2.81) * mm});
            skLineSegment(sketch, "E344.18", {"start": v(32.76, 42.33) * mm, "end": v(2.81, 31.43) * mm});
            skLineSegment(sketch, "E344.19", {"start": v(47.78, -24.15) * mm, "end": v(2.81, -7.78) * mm});
            skLineSegment(sketch, "E344.20", {"start": v(-2.81, -17.46) * mm, "end": v(-50.52, -17.46) * mm});
            skLineSegment(sketch, "E344.21", {"start": v(35.59, -39.98) * mm, "end": v(2.81, -28.05) * mm});
            skLineSegment(sketch, "E344.22", {"start": v(2.81, 41.57) * mm, "end": v(22.3, 48.66) * mm});
            skLineSegment(sketch, "E344.23", {"start": v(-27.12, -46.04) * mm, "end": v(-2.81, -46.04) * mm});
            skLineSegment(sketch, "E344.24", {"start": v(2.81, -38.2) * mm, "end": v(26.18, -46.7) * mm});
            skLineSegment(sketch, "E344.25", {"start": v(26.3, -2.81) * mm, "end": v(17, -2.81) * mm});
            skLineSegment(sketch, "E344.26", {"start": v(2.81, -17.92) * mm, "end": v(42.62, -32.4) * mm});
            skLineSegment(sketch, "E344.27", {"start": v(-2.81, 7.94) * mm, "end": v(-52.85, 7.94) * mm});
            skLineSegment(sketch, "E344.28", {"start": v(2.81, 28.05) * mm, "end": v(35.59, 39.98) * mm});
            skLineSegment(sketch, "E344.29", {"start": v(-44.11, 30.16) * mm, "end": v(-2.81, 30.16) * mm});
            skLineSegment(sketch, "E344.30", {"start": v(-2.81, -42.86) * mm, "end": v(-2.81, -42.86) * mm});
            skLineSegment(sketch, "E344.31", {"start": v(52.74, 9.06) * mm, "end": v(35.58, 2.81) * mm});
            skLineSegment(sketch, "E344.32", {"start": v(2.81, -4.4) * mm, "end": v(49.12, -21.26) * mm});
            skLineSegment(sketch, "E344.33", {"start": v(-52.85, -7.94) * mm, "end": v(-2.81, -7.94) * mm});
            skLineSegment(sketch, "E344.34", {"start": v(-46.12, -26.99) * mm, "end": v(-2.81, -26.99) * mm});
            skLineSegment(sketch, "E344.35", {"start": v(35.58, 2.81) * mm, "end": v(44.86, 2.81) * mm});
            skLineSegment(sketch, "E344.36", {"start": v(-2.81, 33.34) * mm, "end": v(-41.75, 33.34) * mm});
            skLineSegment(sketch, "E344.37", {"start": v(2.81, -44.95) * mm, "end": v(17.91, -50.44) * mm});
            skLineSegment(sketch, "E344.38", {"start": v(44.52, -29.72) * mm, "end": v(2.81, -14.54) * mm});
            skLineSegment(sketch, "E344.39", {"start": v(29.64, -44.57) * mm, "end": v(2.81, -34.81) * mm});
            skLineSegment(sketch, "E344.40", {"start": v(-50.52, 17.46) * mm, "end": v(-2.81, 17.46) * mm});
            skLineSegment(sketch, "E344.41", {"start": v(44.86, 2.81) * mm, "end": v(53.19, 5.84) * mm});
            skLineSegment(sketch, "E344.42", {"start": v(38.16, 37.54) * mm, "end": v(2.81, 24.67) * mm});
            skLineSegment(sketch, "E344.43", {"start": v(-2.81, -4.76) * mm, "end": v(-53.22, -4.76) * mm});
            skLineSegment(sketch, "E344.44", {"start": v(-2.81, -23.81) * mm, "end": v(-47.85, -23.81) * mm});
            skLineSegment(sketch, "E344.45", {"start": v(50.3, -18.3) * mm, "end": v(7.73, -2.81) * mm});
            skLineSegment(sketch, "E344.46", {"start": v(35.58, -2.81) * mm, "end": v(52.74, -9.06) * mm});
            skLineSegment(sketch, "E344.47", {"start": v(2.81, 21.3) * mm, "end": v(40.49, 35) * mm});
            skLineSegment(sketch, "E344.48", {"start": v(-47.85, 23.81) * mm, "end": v(-2.81, 23.81) * mm});
            skLineSegment(sketch, "E344.49", {"start": v(-2.81, 20.64) * mm, "end": v(-49.3, 20.64) * mm});
            skLineSegment(sketch, "E344.50", {"start": v(2.81, -24.67) * mm, "end": v(38.16, -37.54) * mm});
            skLineSegment(sketch, "E344.51", {"start": v(-51.5, -14.29) * mm, "end": v(-2.81, -14.29) * mm});
            skLineSegment(sketch, "E344.52", {"start": v(-31.9, 42.86) * mm, "end": v(-2.81, 42.86) * mm});
            skLineSegment(sketch, "E344.53", {"start": v(49.12, 21.26) * mm, "end": v(2.81, 4.4) * mm});
            skLineSegment(sketch, "E344.54", {"start": v(-41.75, -33.34) * mm, "end": v(-2.81, -33.34) * mm});
            skLineSegment(sketch, "E344.55", {"start": v(22.3, -48.66) * mm, "end": v(2.81, -41.57) * mm});
            skLineSegment(sketch, "E344.56", {"start": v(-2.81, 26.99) * mm, "end": v(-46.12, 26.99) * mm});
            skLineSegment(sketch, "E344.57", {"start": v(-20.83, 49.21) * mm, "end": v(-2.81, 49.21) * mm});
            skLineSegment(sketch, "E344.58", {"start": v(-52.27, 11.11) * mm, "end": v(-2.81, 11.11) * mm});
            skLineSegment(sketch, "E344.59", {"start": v(-53.4, -1.59) * mm, "end": v(-2.81, -1.59) * mm});
            skLineSegment(sketch, "E344.60", {"start": v(53.19, -5.84) * mm, "end": v(44.86, -2.81) * mm});
            skLineSegment(sketch, "E344.61", {"start": v(-2.81, -11.11) * mm, "end": v(-52.27, -11.11) * mm});
            skLineSegment(sketch, "E344.62", {"start": v(-2.81, 46.04) * mm, "end": v(-27.12, 46.04) * mm});
            skLineSegment(sketch, "E344.63", {"start": v(42.62, 32.4) * mm, "end": v(2.81, 17.92) * mm});
            skLineSegment(sketch, "E344.64", {"start": v(40.49, -35) * mm, "end": v(2.81, -21.3) * mm});
            skLineSegment(sketch, "E344.65", {"start": v(-2.81, -30.16) * mm, "end": v(-44.11, -30.16) * mm});
            skLineSegment(sketch, "E344.66", {"start": v(44.86, -2.81) * mm, "end": v(35.58, -2.81) * mm});
            skLineSegment(sketch, "E344.67", {"start": v(26.18, 46.7) * mm, "end": v(2.81, 38.2) * mm});
            skLineSegment(sketch, "E344.68", {"start": v(7.73, 2.81) * mm, "end": v(50.3, 18.3) * mm});
            skLineSegment(sketch, "E344.69", {"start": v(-2.81, 52.39) * mm, "end": v(-10.58, 52.39) * mm});
            skLineSegment(sketch, "E344.70", {"start": v(-2.81, 14.29) * mm, "end": v(-51.5, 14.29) * mm});
            skLineSegment(sketch, "E344.71", {"start": v(-2.81, 1.59) * mm, "end": v(-53.4, 1.59) * mm});
            skLineSegment(sketch, "E344.72", {"start": v(17, -2.81) * mm, "end": v(51.3, -15.3) * mm});
            skLineSegment(sketch, "E344.73", {"start": v(2.81, -11.16) * mm, "end": v(46.24, -26.97) * mm});
            skLineSegment(sketch, "E344.74", {"start": v(2.81, 14.54) * mm, "end": v(44.52, 29.72) * mm});
            skCircle(sketch, "E344.75", {"center": v(0, 0) * mm, "radius": 58.12 * mm});
            skCircle(sketch, "E345", {"center": v(0, 0) * mm, "radius": 53.42 * mm});
            skLineSegment(sketch, "E346", {"start": v(-2.81, 52.39) * mm, "end": v(-2.81, 49.21) * mm});
            skLineSegment(sketch, "E347", {"start": v(-2.81, 46.04) * mm, "end": v(-2.81, 42.86) * mm});
            skLineSegment(sketch, "E348", {"start": v(-2.81, 42.86) * mm, "end": v(-2.81, 42.86) * mm});
            skLineSegment(sketch, "E349", {"start": v(-2.81, 39.69) * mm, "end": v(-35.77, 39.69) * mm});
            skLineSegment(sketch, "E350", {"start": v(-2.81, 33.34) * mm, "end": v(-2.81, 30.16) * mm});
            skLineSegment(sketch, "E351.trimOffspring", {"start": v(-2.81, 39.69) * mm, "end": v(-2.81, 36.51) * mm});
            skLineSegment(sketch, "E352", {"start": v(-2.81, 30.16) * mm, "end": v(-2.81, 30.16) * mm});
            skLineSegment(sketch, "E353", {"start": v(-2.81, 26.99) * mm, "end": v(-2.81, 23.81) * mm});
            skLineSegment(sketch, "E354", {"start": v(-2.81, 20.64) * mm, "end": v(-2.81, 17.46) * mm});
            skLineSegment(sketch, "E355", {"start": v(-2.81, 14.29) * mm, "end": v(-2.81, 11.11) * mm});
            skLineSegment(sketch, "E356", {"start": v(-2.81, 7.94) * mm, "end": v(-2.81, 4.76) * mm});
            skLineSegment(sketch, "E357", {"start": v(-2.81, 1.59) * mm, "end": v(-2.81, -1.59) * mm});
            skLineSegment(sketch, "E358", {"start": v(-2.81, -4.76) * mm, "end": v(-2.81, -7.94) * mm});
            skLineSegment(sketch, "E359", {"start": v(-2.81, -11.11) * mm, "end": v(-2.81, -14.29) * mm});
            skLineSegment(sketch, "E360", {"start": v(-2.81, -17.46) * mm, "end": v(-2.81, -20.64) * mm});
            skLineSegment(sketch, "E361", {"start": v(-2.81, -23.81) * mm, "end": v(-2.81, -26.99) * mm});
            skLineSegment(sketch, "E362", {"start": v(-2.81, -30.16) * mm, "end": v(-2.81, -33.34) * mm});
            skLineSegment(sketch, "E363", {"start": v(-2.81, -36.51) * mm, "end": v(-2.81, -39.69) * mm});
            skLineSegment(sketch, "E364", {"start": v(-2.81, -39.69) * mm, "end": v(-2.81, -39.69) * mm});
            skLineSegment(sketch, "E365", {"start": v(-2.81, -42.86) * mm, "end": v(-31.9, -42.86) * mm});
            skLineSegment(sketch, "E366", {"start": v(-2.81, -42.86) * mm, "end": v(-2.81, -46.04) * mm});
            skLineSegment(sketch, "E367", {"start": v(-2.81, -49.21) * mm, "end": v(-2.81, -52.39) * mm});
            skLineSegment(sketch, "E368.0", {"start": v(2.81, 51.7) * mm, "end": v(2.81, 48.33) * mm});
            skLineSegment(sketch, "E368.1", {"start": v(6.62, 53.1) * mm, "end": v(2.81, 51.7) * mm});
            skLineSegment(sketch, "E369.0", {"start": v(7.73, -2.81) * mm, "end": v(2.81, -2.81) * mm});
            skLineSegment(sketch, "E369.1", {"start": v(2.81, 2.81) * mm, "end": v(7.73, 2.81) * mm});
            skLineSegment(sketch, "E370.0", {"start": v(2.81, 38.2) * mm, "end": v(2.81, 34.81) * mm});
            skLineSegment(sketch, "E371.0", {"start": v(2.81, 44.95) * mm, "end": v(2.81, 41.57) * mm});
            skLineSegment(sketch, "E372.0", {"start": v(2.81, 31.43) * mm, "end": v(2.81, 28.05) * mm});
            skLineSegment(sketch, "E373.0", {"start": v(2.81, 4.4) * mm, "end": v(2.81, 2.81) * mm});
            skLineSegment(sketch, "E374.0", {"start": v(2.81, 11.16) * mm, "end": v(2.81, 7.78) * mm});
            skLineSegment(sketch, "E375.0", {"start": v(2.81, 17.92) * mm, "end": v(2.81, 14.54) * mm});
            skLineSegment(sketch, "E376.0", {"start": v(2.81, 24.67) * mm, "end": v(2.81, 21.3) * mm});
            skLineSegment(sketch, "E377.0", {"start": v(2.81, -2.81) * mm, "end": v(2.81, -4.4) * mm});
            skLineSegment(sketch, "E378.0", {"start": v(2.81, -7.78) * mm, "end": v(2.81, -11.16) * mm});
            skLineSegment(sketch, "E379.0", {"start": v(2.81, -14.54) * mm, "end": v(2.81, -17.92) * mm});
            skLineSegment(sketch, "E380.0", {"start": v(2.81, -21.3) * mm, "end": v(2.81, -24.67) * mm});
            skLineSegment(sketch, "E381.0", {"start": v(12.82, -51.97) * mm, "end": v(2.81, -48.33) * mm});
            skLineSegment(sketch, "E382.0", {"start": v(2.81, -51.7) * mm, "end": v(6.62, -53.1) * mm});
            skLineSegment(sketch, "E383.0", {"start": v(2.81, -48.33) * mm, "end": v(2.81, -51.7) * mm});
            skLineSegment(sketch, "E384.0", {"start": v(2.81, -41.57) * mm, "end": v(2.81, -44.95) * mm});
            skLineSegment(sketch, "E385.0", {"start": v(2.81, -34.81) * mm, "end": v(2.81, -38.2) * mm});
            skLineSegment(sketch, "E386.0", {"start": v(2.81, -28.05) * mm, "end": v(2.81, -31.43) * mm});
            skCircle(sketch, "E387.0", {"center": v(0, 0) * mm, "radius": 61.5 * mm, "construction": true});
            skCircle(sketch, "E388.0", {"center": v(0, 0) * mm, "radius": 72 * mm});
            skCircle(sketch, "E389.0", {"center": v(0, 0) * mm, "radius": 60.5 * mm});
            skLineSegment(sketch, "E390", {"start": v(0, 0) * mm, "end": v(0, 70.81) * mm, "construction": true});
            skArc(sketch, "E391", {"start": v(-1, 60.5) * mm, "mid": v(0, 59.5) * mm, "end": v(1, 60.5) * mm, "construction": true});
            skArc(sketch, "E392", {"start": v(1, 60.5) * mm, "mid": v(0, 61.5) * mm, "end": v(-1, 60.5) * mm});
            skArc(sketch, "E393.1.0", {"start": v(-60.5, -1) * mm, "mid": v(-59.5, 0) * mm, "end": v(-60.5, 1) * mm, "construction": true});
            skArc(sketch, "E393.1.1", {"start": v(-60.5, 1) * mm, "mid": v(-61.5, 0) * mm, "end": v(-60.5, -1) * mm});
            skArc(sketch, "E393.2.0", {"start": v(1, -60.5) * mm, "mid": v(0, -59.5) * mm, "end": v(-1, -60.5) * mm, "construction": true});
            skArc(sketch, "E393.2.1", {"start": v(-1, -60.5) * mm, "mid": v(0, -61.5) * mm, "end": v(1, -60.5) * mm});
            skArc(sketch, "E394.2.3.0", {"start": v(60.5, 1) * mm, "mid": v(59.5, 0) * mm, "end": v(60.5, -1) * mm, "construction": true});
            skArc(sketch, "E394.4.3.0", {"start": v(60.5, -1) * mm, "mid": v(61.5, 0) * mm, "end": v(60.5, 1) * mm});
            skSolve(sketch);
        }
        {
            var Q0;
            {var subQ12=sQuery(id+"F2.wireOp",EDGE,"E346");Q0=makeQuery(id+"F2.imprint","IMPRINT",FACE,{"disambiguationData":[TD([[makeQuery(id+"F2.imprint","IMPRINT",EDGE,{"derivedFrom":subQ12}),1.0]])]});}
            extrude(context, id + "F3", {"entities" : qUnion([Q0]), "depth" : 25 * mm, "offsetDistance" : 25 * mm});
        }
        {
            var Q0;
            {var subQ119=sQuery(id+"F2.wireOp",EDGE,"E344.9");Q0=makeQuery(id+"F2.imprint","IMPRINT",FACE,{"disambiguationData":[TD([[makeQuery(id+"F2.imprint","IMPRINT",EDGE,{"derivedFrom":subQ119}),-1.0]])]});}
            var Q1;
            Q1=makeQuery(id+"F2.imprint","IMPRINT",FACE,{"disambiguationData":[TD([[makeQuery(id+"F2.imprint","IMPRINT",EDGE,{"derivedFrom":sQuery(id+"F2.wireOp",EDGE,"E344.75")}),1.0]])]});
            var Q2;
            Q2=makeQuery(id+"F2.imprint","IMPRINT",FACE,{"disambiguationData":[TD([[makeQuery(id+"F2.imprint","IMPRINT",EDGE,{"derivedFrom":sQuery(id+"F2.wireOp",EDGE,"E387.0")}),-1.0]])]});
            extrude(context, id + "F4", {"entities" : qUnion([Q0, Q1, Q2]), "oppositeDirection" : true, "depth" : 2 * mm, "offsetDistance" : 25 * mm});
        }
        {
            var Q0;
            Q0=makeQuery(id+"F2.imprint","IMPRINT",FACE,{"disambiguationData":[TD([[makeQuery(id+"F2.imprint","IMPRINT",EDGE,{"derivedFrom":sQuery(id+"F2.wireOp",EDGE,"E344.75")}),-1.0]])]});
            var Q1;
            {var subQ0=sQuery(id+"F2.wireOp",EDGE,"E392");Q1=makeQuery(id+"F2.imprint","IMPRINT",FACE,{"disambiguationData":[TD([[makeQuery(id+"F2.imprint","IMPRINT",EDGE,{"derivedFrom":subQ0}),1.0]])]});}
            var Q2;
            {var subQ0=sQuery(id+"F2.wireOp",EDGE,"E394.4.3.0");Q2=makeQuery(id+"F2.imprint","IMPRINT",FACE,{"disambiguationData":[TD([[makeQuery(id+"F2.imprint","IMPRINT",EDGE,{"derivedFrom":subQ0}),1.0]])]});}
            var Q3;
            {var subQ0=sQuery(id+"F2.wireOp",EDGE,"E393.2.1");Q3=makeQuery(id+"F2.imprint","IMPRINT",FACE,{"disambiguationData":[TD([[makeQuery(id+"F2.imprint","IMPRINT",EDGE,{"derivedFrom":subQ0}),1.0]])]});}
            var Q4;
            {var subQ0=sQuery(id+"F2.wireOp",EDGE,"E393.1.1");Q4=makeQuery(id+"F2.imprint","IMPRINT",FACE,{"disambiguationData":[TD([[makeQuery(id+"F2.imprint","IMPRINT",EDGE,{"derivedFrom":subQ0}),1.0]])]});}
            var Q5;
            Q5=makeQuery(id+"F4.opExtrude","CAP_FACE",FACE,{"disambiguationData":[OSD([sQuery(id+"F2.wireOp",EDGE,"E344.0"),sQuery(id+"F2.wireOp",EDGE,"E344.1"),sQuery(id+"F2.wireOp",EDGE,"E344.2"),sQuery(id+"F2.wireOp",EDGE,"E344.3"),sQuery(id+"F2.wireOp",EDGE,"E344.4"),sQuery(id+"F2.wireOp",EDGE,"E344.5"),sQuery(id+"F2.wireOp",EDGE,"E344.6"),sQuery(id+"F2.wireOp",EDGE,"E344.7"),sQuery(id+"F2.wireOp",EDGE,"E344.8"),sQuery(id+"F2.wireOp",EDGE,"E344.9"),sQuery(id+"F2.wireOp",EDGE,"E344.10"),sQuery(id+"F2.wireOp",EDGE,"E344.11"),sQuery(id+"F2.wireOp",EDGE,"E344.12"),sQuery(id+"F2.wireOp",EDGE,"E344.13"),sQuery(id+"F2.wireOp",EDGE,"E344.15"),sQuery(id+"F2.wireOp",EDGE,"E344.16"),sQuery(id+"F2.wireOp",EDGE,"E344.17"),sQuery(id+"F2.wireOp",EDGE,"E344.18"),sQuery(id+"F2.wireOp",EDGE,"E344.19"),sQuery(id+"F2.wireOp",EDGE,"E344.20"),sQuery(id+"F2.wireOp",EDGE,"E344.21"),sQuery(id+"F2.wireOp",EDGE,"E344.22"),sQuery(id+"F2.wireOp",EDGE,"E344.23"),sQuery(id+"F2.wireOp",EDGE,"E344.24"),sQuery(id+"F2.wireOp",EDGE,"E344.25"),sQuery(id+"F2.wireOp",EDGE,"E344.26"),sQuery(id+"F2.wireOp",EDGE,"E344.27"),sQuery(id+"F2.wireOp",EDGE,"E344.28"),sQuery(id+"F2.wireOp",EDGE,"E344.29"),sQuery(id+"F2.wireOp",EDGE,"E344.31"),sQuery(id+"F2.wireOp",EDGE,"E344.32"),sQuery(id+"F2.wireOp",EDGE,"E344.33"),sQuery(id+"F2.wireOp",EDGE,"E344.34"),sQuery(id+"F2.wireOp",EDGE,"E344.35"),sQuery(id+"F2.wireOp",EDGE,"E344.36"),sQuery(id+"F2.wireOp",EDGE,"E344.37"),sQuery(id+"F2.wireOp",EDGE,"E344.38"),sQuery(id+"F2.wireOp",EDGE,"E344.39"),sQuery(id+"F2.wireOp",EDGE,"E344.40"),sQuery(id+"F2.wireOp",EDGE,"E344.41"),sQuery(id+"F2.wireOp",EDGE,"E344.42"),sQuery(id+"F2.wireOp",EDGE,"E344.43"),sQuery(id+"F2.wireOp",EDGE,"E344.44"),sQuery(id+"F2.wireOp",EDGE,"E344.45"),sQuery(id+"F2.wireOp",EDGE,"E344.46"),sQuery(id+"F2.wireOp",EDGE,"E344.47"),sQuery(id+"F2.wireOp",EDGE,"E344.48"),sQuery(id+"F2.wireOp",EDGE,"E344.49"),sQuery(id+"F2.wireOp",EDGE,"E344.50"),sQuery(id+"F2.wireOp",EDGE,"E344.51"),sQuery(id+"F2.wireOp",EDGE,"E344.52"),sQuery(id+"F2.wireOp",EDGE,"E344.53"),sQuery(id+"F2.wireOp",EDGE,"E344.54"),sQuery(id+"F2.wireOp",EDGE,"E344.55"),sQuery(id+"F2.wireOp",EDGE,"E344.56"),sQuery(id+"F2.wireOp",EDGE,"E344.57"),sQuery(id+"F2.wireOp",EDGE,"E344.58"),sQuery(id+"F2.wireOp",EDGE,"E344.59"),sQuery(id+"F2.wireOp",EDGE,"E344.60"),sQuery(id+"F2.wireOp",EDGE,"E344.61"),sQuery(id+"F2.wireOp",EDGE,"E344.62"),sQuery(id+"F2.wireOp",EDGE,"E344.63"),sQuery(id+"F2.wireOp",EDGE,"E344.64"),sQuery(id+"F2.wireOp",EDGE,"E344.65"),sQuery(id+"F2.wireOp",EDGE,"E344.66"),sQuery(id+"F2.wireOp",EDGE,"E344.67"),sQuery(id+"F2.wireOp",EDGE,"E344.68"),sQuery(id+"F2.wireOp",EDGE,"E344.69"),sQuery(id+"F2.wireOp",EDGE,"E344.70"),sQuery(id+"F2.wireOp",EDGE,"E344.71"),sQuery(id+"F2.wireOp",EDGE,"E344.72"),sQuery(id+"F2.wireOp",EDGE,"E344.73"),sQuery(id+"F2.wireOp",EDGE,"E344.74"),sQuery(id+"F2.wireOp",EDGE,"E344.75"),sQuery(id+"F2.wireOp",EDGE,"E345"),sQuery(id+"F2.wireOp",EDGE,"E346"),sQuery(id+"F2.wireOp",EDGE,"E347"),sQuery(id+"F2.wireOp",EDGE,"E349"),sQuery(id+"F2.wireOp",EDGE,"E350"),sQuery(id+"F2.wireOp",EDGE,"E351.trimOffspring"),sQuery(id+"F2.wireOp",EDGE,"E353"),sQuery(id+"F2.wireOp",EDGE,"E354"),sQuery(id+"F2.wireOp",EDGE,"E355"),sQuery(id+"F2.wireOp",EDGE,"E356"),sQuery(id+"F2.wireOp",EDGE,"E357"),sQuery(id+"F2.wireOp",EDGE,"E358"),sQuery(id+"F2.wireOp",EDGE,"E359"),sQuery(id+"F2.wireOp",EDGE,"E360"),sQuery(id+"F2.wireOp",EDGE,"E361"),sQuery(id+"F2.wireOp",EDGE,"E362"),sQuery(id+"F2.wireOp",EDGE,"E363"),sQuery(id+"F2.wireOp",EDGE,"E365"),sQuery(id+"F2.wireOp",EDGE,"E366"),sQuery(id+"F2.wireOp",EDGE,"E367"),sQuery(id+"F2.wireOp",EDGE,"E368.0"),sQuery(id+"F2.wireOp",EDGE,"E368.1"),sQuery(id+"F2.wireOp",EDGE,"E369.0"),sQuery(id+"F2.wireOp",EDGE,"E369.1"),sQuery(id+"F2.wireOp",EDGE,"E370.0"),sQuery(id+"F2.wireOp",EDGE,"E371.0"),sQuery(id+"F2.wireOp",EDGE,"E372.0"),sQuery(id+"F2.wireOp",EDGE,"E373.0"),sQuery(id+"F2.wireOp",EDGE,"E374.0"),sQuery(id+"F2.wireOp",EDGE,"E375.0"),sQuery(id+"F2.wireOp",EDGE,"E376.0"),sQuery(id+"F2.wireOp",EDGE,"E377.0"),sQuery(id+"F2.wireOp",EDGE,"E378.0"),sQuery(id+"F2.wireOp",EDGE,"E379.0"),sQuery(id+"F2.wireOp",EDGE,"E380.0"),sQuery(id+"F2.wireOp",EDGE,"E381.0"),sQuery(id+"F2.wireOp",EDGE,"E382.0"),sQuery(id+"F2.wireOp",EDGE,"E383.0"),sQuery(id+"F2.wireOp",EDGE,"E384.0"),sQuery(id+"F2.wireOp",EDGE,"E385.0"),sQuery(id+"F2.wireOp",EDGE,"E386.0")])],"isStart":false});
            extrude(context, id + "F5", {"entities" : qUnion([Q0, Q1, Q2, Q3, Q4]), "operationType" : NewBodyOperationType.ADD, "depth" : 10 * mm, "offsetDistance" : 25 * mm, "hasSecondDirection" : true, "secondDirectionBound" : SecondDirectionBoundingType.UP_TO_SURFACE, "secondDirectionOppositeDirection" : true, "secondDirectionDepth" : 25 * mm, "secondDirectionBoundEntityFace" : qUnion([Q5])});
        }
        {
            var Q0;
            Q0=makeQuery(id+"F3.opExtrude","SWEPT_BODY",BODY,{"disambiguationData":[OSD([sQuery(id+"F2.wireOp",EDGE,"E344.0"),sQuery(id+"F2.wireOp",EDGE,"E344.1"),sQuery(id+"F2.wireOp",EDGE,"E344.2"),sQuery(id+"F2.wireOp",EDGE,"E344.3"),sQuery(id+"F2.wireOp",EDGE,"E344.4"),sQuery(id+"F2.wireOp",EDGE,"E344.5"),sQuery(id+"F2.wireOp",EDGE,"E344.6"),sQuery(id+"F2.wireOp",EDGE,"E344.7"),sQuery(id+"F2.wireOp",EDGE,"E344.8"),sQuery(id+"F2.wireOp",EDGE,"E344.9"),sQuery(id+"F2.wireOp",EDGE,"E344.10"),sQuery(id+"F2.wireOp",EDGE,"E344.11"),sQuery(id+"F2.wireOp",EDGE,"E344.12"),sQuery(id+"F2.wireOp",EDGE,"E344.13"),sQuery(id+"F2.wireOp",EDGE,"E344.15"),sQuery(id+"F2.wireOp",EDGE,"E344.16"),sQuery(id+"F2.wireOp",EDGE,"E344.17"),sQuery(id+"F2.wireOp",EDGE,"E344.18"),sQuery(id+"F2.wireOp",EDGE,"E344.19"),sQuery(id+"F2.wireOp",EDGE,"E344.20"),sQuery(id+"F2.wireOp",EDGE,"E344.21"),sQuery(id+"F2.wireOp",EDGE,"E344.22"),sQuery(id+"F2.wireOp",EDGE,"E344.23"),sQuery(id+"F2.wireOp",EDGE,"E344.24"),sQuery(id+"F2.wireOp",EDGE,"E344.25"),sQuery(id+"F2.wireOp",EDGE,"E344.26"),sQuery(id+"F2.wireOp",EDGE,"E344.27"),sQuery(id+"F2.wireOp",EDGE,"E344.28"),sQuery(id+"F2.wireOp",EDGE,"E344.29"),sQuery(id+"F2.wireOp",EDGE,"E344.31"),sQuery(id+"F2.wireOp",EDGE,"E344.32"),sQuery(id+"F2.wireOp",EDGE,"E344.33"),sQuery(id+"F2.wireOp",EDGE,"E344.34"),sQuery(id+"F2.wireOp",EDGE,"E344.35"),sQuery(id+"F2.wireOp",EDGE,"E344.36"),sQuery(id+"F2.wireOp",EDGE,"E344.37"),sQuery(id+"F2.wireOp",EDGE,"E344.38"),sQuery(id+"F2.wireOp",EDGE,"E344.39"),sQuery(id+"F2.wireOp",EDGE,"E344.40"),sQuery(id+"F2.wireOp",EDGE,"E344.41"),sQuery(id+"F2.wireOp",EDGE,"E344.42"),sQuery(id+"F2.wireOp",EDGE,"E344.43"),sQuery(id+"F2.wireOp",EDGE,"E344.44"),sQuery(id+"F2.wireOp",EDGE,"E344.45"),sQuery(id+"F2.wireOp",EDGE,"E344.46"),sQuery(id+"F2.wireOp",EDGE,"E344.47"),sQuery(id+"F2.wireOp",EDGE,"E344.48"),sQuery(id+"F2.wireOp",EDGE,"E344.49"),sQuery(id+"F2.wireOp",EDGE,"E344.50"),sQuery(id+"F2.wireOp",EDGE,"E344.51"),sQuery(id+"F2.wireOp",EDGE,"E344.52"),sQuery(id+"F2.wireOp",EDGE,"E344.53"),sQuery(id+"F2.wireOp",EDGE,"E344.54"),sQuery(id+"F2.wireOp",EDGE,"E344.55"),sQuery(id+"F2.wireOp",EDGE,"E344.56"),sQuery(id+"F2.wireOp",EDGE,"E344.57"),sQuery(id+"F2.wireOp",EDGE,"E344.58"),sQuery(id+"F2.wireOp",EDGE,"E344.59"),sQuery(id+"F2.wireOp",EDGE,"E344.60"),sQuery(id+"F2.wireOp",EDGE,"E344.61"),sQuery(id+"F2.wireOp",EDGE,"E344.62"),sQuery(id+"F2.wireOp",EDGE,"E344.63"),sQuery(id+"F2.wireOp",EDGE,"E344.64"),sQuery(id+"F2.wireOp",EDGE,"E344.65"),sQuery(id+"F2.wireOp",EDGE,"E344.66"),sQuery(id+"F2.wireOp",EDGE,"E344.67"),sQuery(id+"F2.wireOp",EDGE,"E344.68"),sQuery(id+"F2.wireOp",EDGE,"E344.69"),sQuery(id+"F2.wireOp",EDGE,"E344.70"),sQuery(id+"F2.wireOp",EDGE,"E344.71"),sQuery(id+"F2.wireOp",EDGE,"E344.72"),sQuery(id+"F2.wireOp",EDGE,"E344.73"),sQuery(id+"F2.wireOp",EDGE,"E344.74"),sQuery(id+"F2.wireOp",EDGE,"E345"),sQuery(id+"F2.wireOp",EDGE,"E346"),sQuery(id+"F2.wireOp",EDGE,"E347"),sQuery(id+"F2.wireOp",EDGE,"E349"),sQuery(id+"F2.wireOp",EDGE,"E350"),sQuery(id+"F2.wireOp",EDGE,"E351.trimOffspring"),sQuery(id+"F2.wireOp",EDGE,"E353"),sQuery(id+"F2.wireOp",EDGE,"E354"),sQuery(id+"F2.wireOp",EDGE,"E355"),sQuery(id+"F2.wireOp",EDGE,"E356"),sQuery(id+"F2.wireOp",EDGE,"E357"),sQuery(id+"F2.wireOp",EDGE,"E358"),sQuery(id+"F2.wireOp",EDGE,"E359"),sQuery(id+"F2.wireOp",EDGE,"E360"),sQuery(id+"F2.wireOp",EDGE,"E361"),sQuery(id+"F2.wireOp",EDGE,"E362"),sQuery(id+"F2.wireOp",EDGE,"E363"),sQuery(id+"F2.wireOp",EDGE,"E365"),sQuery(id+"F2.wireOp",EDGE,"E366"),sQuery(id+"F2.wireOp",EDGE,"E367"),sQuery(id+"F2.wireOp",EDGE,"E368.0"),sQuery(id+"F2.wireOp",EDGE,"E368.1"),sQuery(id+"F2.wireOp",EDGE,"E369.0"),sQuery(id+"F2.wireOp",EDGE,"E369.1"),sQuery(id+"F2.wireOp",EDGE,"E370.0"),sQuery(id+"F2.wireOp",EDGE,"E371.0"),sQuery(id+"F2.wireOp",EDGE,"E372.0"),sQuery(id+"F2.wireOp",EDGE,"E373.0"),sQuery(id+"F2.wireOp",EDGE,"E374.0"),sQuery(id+"F2.wireOp",EDGE,"E375.0"),sQuery(id+"F2.wireOp",EDGE,"E376.0"),sQuery(id+"F2.wireOp",EDGE,"E377.0"),sQuery(id+"F2.wireOp",EDGE,"E378.0"),sQuery(id+"F2.wireOp",EDGE,"E379.0"),sQuery(id+"F2.wireOp",EDGE,"E380.0"),sQuery(id+"F2.wireOp",EDGE,"E381.0"),sQuery(id+"F2.wireOp",EDGE,"E382.0"),sQuery(id+"F2.wireOp",EDGE,"E383.0"),sQuery(id+"F2.wireOp",EDGE,"E384.0"),sQuery(id+"F2.wireOp",EDGE,"E385.0"),sQuery(id+"F2.wireOp",EDGE,"E386.0")])]});
            deleteBodies(context, id + "F6", {"entities" : qUnion([Q0])});
        }
        {
            var Q0;
            Q0=makeQuery(id+"F2.imprint","IMPRINT",FACE,{"disambiguationData":[TD([[makeQuery(id+"F2.imprint","IMPRINT",EDGE,{"derivedFrom":sQuery(id+"F2.wireOp",EDGE,"E388.0")}),1.0]])]});
            var Q1;
            {var subQ0=sQuery(id+"F2.wireOp",EDGE,"E344.75");Q1=makeQuery(id+"F5.boolean.opBoolean","MERGE",FACE,{"derivedFrom":[makeQuery(id+"F4.opExtrude","CAP_FACE",FACE,{"disambiguationData":[OSD([sQuery(id+"F2.wireOp",EDGE,"E344.0"),sQuery(id+"F2.wireOp",EDGE,"E344.1"),sQuery(id+"F2.wireOp",EDGE,"E344.2"),sQuery(id+"F2.wireOp",EDGE,"E344.3"),sQuery(id+"F2.wireOp",EDGE,"E344.4"),sQuery(id+"F2.wireOp",EDGE,"E344.5"),sQuery(id+"F2.wireOp",EDGE,"E344.6"),sQuery(id+"F2.wireOp",EDGE,"E344.7"),sQuery(id+"F2.wireOp",EDGE,"E344.8"),sQuery(id+"F2.wireOp",EDGE,"E344.9"),sQuery(id+"F2.wireOp",EDGE,"E344.10"),sQuery(id+"F2.wireOp",EDGE,"E344.11"),sQuery(id+"F2.wireOp",EDGE,"E344.12"),sQuery(id+"F2.wireOp",EDGE,"E344.13"),sQuery(id+"F2.wireOp",EDGE,"E344.15"),sQuery(id+"F2.wireOp",EDGE,"E344.16"),sQuery(id+"F2.wireOp",EDGE,"E344.17"),sQuery(id+"F2.wireOp",EDGE,"E344.18"),sQuery(id+"F2.wireOp",EDGE,"E344.19"),sQuery(id+"F2.wireOp",EDGE,"E344.20"),sQuery(id+"F2.wireOp",EDGE,"E344.21"),sQuery(id+"F2.wireOp",EDGE,"E344.22"),sQuery(id+"F2.wireOp",EDGE,"E344.23"),sQuery(id+"F2.wireOp",EDGE,"E344.24"),sQuery(id+"F2.wireOp",EDGE,"E344.25"),sQuery(id+"F2.wireOp",EDGE,"E344.26"),sQuery(id+"F2.wireOp",EDGE,"E344.27"),sQuery(id+"F2.wireOp",EDGE,"E344.28"),sQuery(id+"F2.wireOp",EDGE,"E344.29"),sQuery(id+"F2.wireOp",EDGE,"E344.31"),sQuery(id+"F2.wireOp",EDGE,"E344.32"),sQuery(id+"F2.wireOp",EDGE,"E344.33"),sQuery(id+"F2.wireOp",EDGE,"E344.34"),sQuery(id+"F2.wireOp",EDGE,"E344.35"),sQuery(id+"F2.wireOp",EDGE,"E344.36"),sQuery(id+"F2.wireOp",EDGE,"E344.37"),sQuery(id+"F2.wireOp",EDGE,"E344.38"),sQuery(id+"F2.wireOp",EDGE,"E344.39"),sQuery(id+"F2.wireOp",EDGE,"E344.40"),sQuery(id+"F2.wireOp",EDGE,"E344.41"),sQuery(id+"F2.wireOp",EDGE,"E344.42"),sQuery(id+"F2.wireOp",EDGE,"E344.43"),sQuery(id+"F2.wireOp",EDGE,"E344.44"),sQuery(id+"F2.wireOp",EDGE,"E344.45"),sQuery(id+"F2.wireOp",EDGE,"E344.46"),sQuery(id+"F2.wireOp",EDGE,"E344.47"),sQuery(id+"F2.wireOp",EDGE,"E344.48"),sQuery(id+"F2.wireOp",EDGE,"E344.49"),sQuery(id+"F2.wireOp",EDGE,"E344.50"),sQuery(id+"F2.wireOp",EDGE,"E344.51"),sQuery(id+"F2.wireOp",EDGE,"E344.52"),sQuery(id+"F2.wireOp",EDGE,"E344.53"),sQuery(id+"F2.wireOp",EDGE,"E344.54"),sQuery(id+"F2.wireOp",EDGE,"E344.55"),sQuery(id+"F2.wireOp",EDGE,"E344.56"),sQuery(id+"F2.wireOp",EDGE,"E344.57"),sQuery(id+"F2.wireOp",EDGE,"E344.58"),sQuery(id+"F2.wireOp",EDGE,"E344.59"),sQuery(id+"F2.wireOp",EDGE,"E344.60"),sQuery(id+"F2.wireOp",EDGE,"E344.61"),sQuery(id+"F2.wireOp",EDGE,"E344.62"),sQuery(id+"F2.wireOp",EDGE,"E344.63"),sQuery(id+"F2.wireOp",EDGE,"E344.64"),sQuery(id+"F2.wireOp",EDGE,"E344.65"),sQuery(id+"F2.wireOp",EDGE,"E344.66"),sQuery(id+"F2.wireOp",EDGE,"E344.67"),sQuery(id+"F2.wireOp",EDGE,"E344.68"),sQuery(id+"F2.wireOp",EDGE,"E344.69"),sQuery(id+"F2.wireOp",EDGE,"E344.70"),sQuery(id+"F2.wireOp",EDGE,"E344.71"),sQuery(id+"F2.wireOp",EDGE,"E344.72"),sQuery(id+"F2.wireOp",EDGE,"E344.73"),sQuery(id+"F2.wireOp",EDGE,"E344.74"),subQ0,sQuery(id+"F2.wireOp",EDGE,"E345"),sQuery(id+"F2.wireOp",EDGE,"E346"),sQuery(id+"F2.wireOp",EDGE,"E347"),sQuery(id+"F2.wireOp",EDGE,"E349"),sQuery(id+"F2.wireOp",EDGE,"E350"),sQuery(id+"F2.wireOp",EDGE,"E351.trimOffspring"),sQuery(id+"F2.wireOp",EDGE,"E353"),sQuery(id+"F2.wireOp",EDGE,"E354"),sQuery(id+"F2.wireOp",EDGE,"E355"),sQuery(id+"F2.wireOp",EDGE,"E356"),sQuery(id+"F2.wireOp",EDGE,"E357"),sQuery(id+"F2.wireOp",EDGE,"E358"),sQuery(id+"F2.wireOp",EDGE,"E359"),sQuery(id+"F2.wireOp",EDGE,"E360"),sQuery(id+"F2.wireOp",EDGE,"E361"),sQuery(id+"F2.wireOp",EDGE,"E362"),sQuery(id+"F2.wireOp",EDGE,"E363"),sQuery(id+"F2.wireOp",EDGE,"E365"),sQuery(id+"F2.wireOp",EDGE,"E366"),sQuery(id+"F2.wireOp",EDGE,"E367"),sQuery(id+"F2.wireOp",EDGE,"E368.0"),sQuery(id+"F2.wireOp",EDGE,"E368.1"),sQuery(id+"F2.wireOp",EDGE,"E369.0"),sQuery(id+"F2.wireOp",EDGE,"E369.1"),sQuery(id+"F2.wireOp",EDGE,"E370.0"),sQuery(id+"F2.wireOp",EDGE,"E371.0"),sQuery(id+"F2.wireOp",EDGE,"E372.0"),sQuery(id+"F2.wireOp",EDGE,"E373.0"),sQuery(id+"F2.wireOp",EDGE,"E374.0"),sQuery(id+"F2.wireOp",EDGE,"E375.0"),sQuery(id+"F2.wireOp",EDGE,"E376.0"),sQuery(id+"F2.wireOp",EDGE,"E377.0"),sQuery(id+"F2.wireOp",EDGE,"E378.0"),sQuery(id+"F2.wireOp",EDGE,"E379.0"),sQuery(id+"F2.wireOp",EDGE,"E380.0"),sQuery(id+"F2.wireOp",EDGE,"E381.0"),sQuery(id+"F2.wireOp",EDGE,"E382.0"),sQuery(id+"F2.wireOp",EDGE,"E383.0"),sQuery(id+"F2.wireOp",EDGE,"E384.0"),sQuery(id+"F2.wireOp",EDGE,"E385.0"),sQuery(id+"F2.wireOp",EDGE,"E386.0")])],"isStart":false}),makeQuery(id+"F5.opExtrude","CAP_FACE",FACE,{"disambiguationData":[OSD([subQ0,sQuery(id+"F2.wireOp",EDGE,"E389.0"),sQuery(id+"F2.wireOp",EDGE,"E392"),sQuery(id+"F2.wireOp",EDGE,"E393.1.1"),sQuery(id+"F2.wireOp",EDGE,"E393.2.1"),sQuery(id+"F2.wireOp",EDGE,"E394.4.3.0")])],"isStart":true})]});}
            extrude(context, id + "F7", {"entities" : qUnion([Q0]), "operationType" : NewBodyOperationType.ADD, "endBound" : BoundingType.UP_TO_SURFACE, "oppositeDirection" : true, "depth" : 25 * mm, "endBoundEntityFace" : qUnion([Q1]), "offsetDistance" : 25 * mm});
        }
    });
